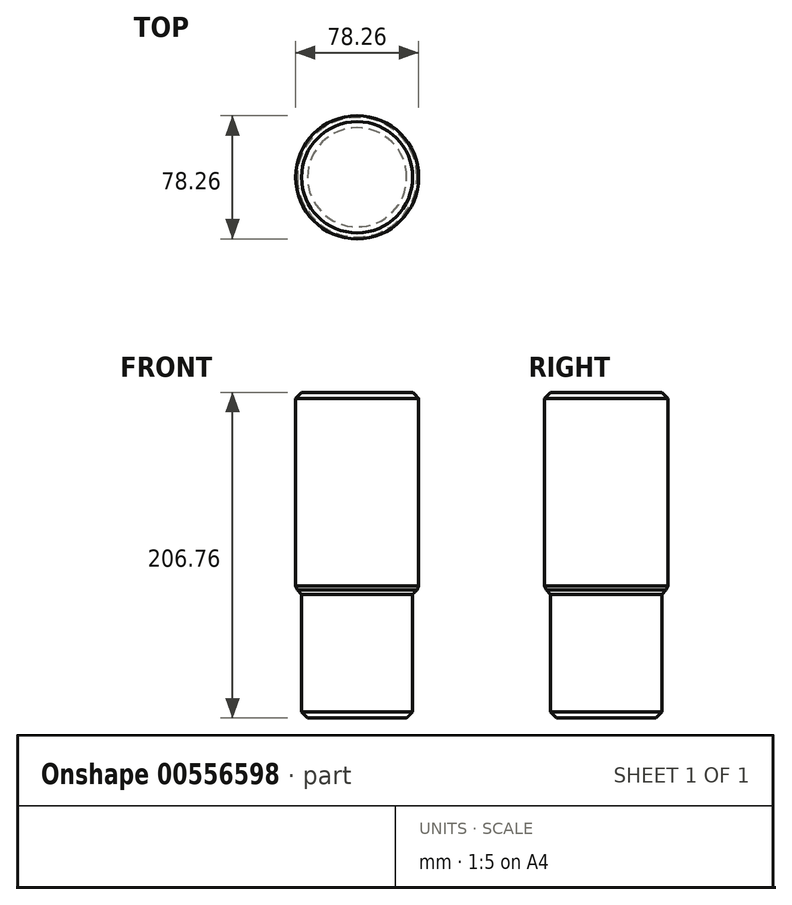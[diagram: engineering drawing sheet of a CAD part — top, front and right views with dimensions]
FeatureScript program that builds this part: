
annotation { "Feature Type Name" : "Feature", "Feature Type Description" : "" }
export const myFeature = defineFeature(function(context is Context, id is Id, definition is map)
    precondition{}
    {
        {
            var Q0;
            Q0=qCreatedBy(makeId("Top.planeOp"),FACE);
            var sketch = newSketch(context, id + "F0", { "sketchPlane" : qUnion([Q0])});
            skCircle(sketch, "E0", {"center": v(0, 0) * mm, "radius": 39.13 * mm});
            skSolve(sketch);
        }
        {
            var Q0;
            Q0 = qSketchRegion(id + "F0", true);
            extrude(context, id + "F1", {"entities" : qUnion([Q0]), "depth" : 124.46 * mm, "offsetDistance" : 25.4 * mm});
        }
        {
            var Q0;
            Q0=qCreatedBy(makeId("Top.planeOp"),FACE);
            var sketch = newSketch(context, id + "F2", { "sketchPlane" : qUnion([Q0])});
            skCircle(sketch, "E1", {"center": v(0, 0) * mm, "radius": 35.32 * mm});
            skSolve(sketch);
        }
        {
            var Q0;
            Q0 = qSketchRegion(id + "F2", true);
            extrude(context, id + "F3", {"entities" : qUnion([Q0]), "operationType" : NewBodyOperationType.ADD, "oppositeDirection" : true, "depth" : 82.3 * mm, "offsetDistance" : 25.4 * mm});
        }
        {
            var Q0;
            Q0=makeQuery(id+"F3.opExtrude","CAP_FACE",FACE,{"disambiguationData":[OSD([sQuery(id+"F2.wireOp",EDGE,"E1")])],"isStart":false});
            var Q1;
            Q1=makeQuery(id+"F3.opExtrude","SWEPT_FACE",FACE,{"disambiguationData":[OSD([sQuery(id+"F2.wireOp",EDGE,"E1")])]});
            chamfer(context, id + "F4", {"entities" : qUnion([Q0, Q1]), "width" : 3.8 * mm, "tangentPropagation" : true});
        }
        {
            var Q0;
            Q0=makeQuery(id+"F1.opExtrude","SWEPT_FACE",FACE,{"disambiguationData":[OSD([sQuery(id+"F0.wireOp",EDGE,"E0")])]});
            var Q1;
            Q1=makeQuery(id+"F1.opExtrude","CAP_EDGE",EDGE,{"disambiguationData":[OSD([sQuery(id+"F0.wireOp",EDGE,"E0")])],"isStart":false});
            chamfer(context, id + "F5", {"entities" : qUnion([Q0, Q1]), "width" : 3.8 * mm, "tangentPropagation" : true});
        }
    });
